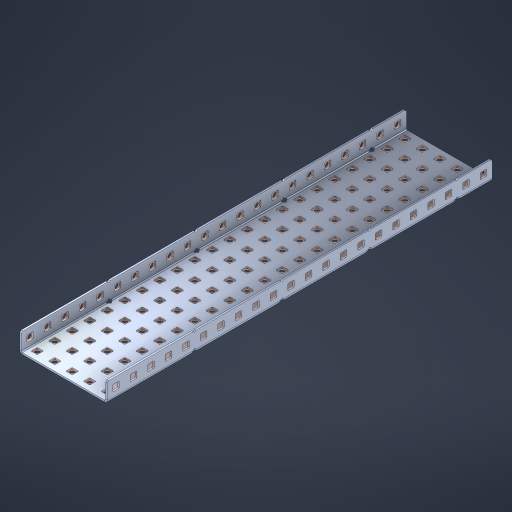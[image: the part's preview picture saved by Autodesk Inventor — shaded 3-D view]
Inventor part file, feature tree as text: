
AUTODESK INVENTOR PART (.ipt)
format: ipt  version: 2023 (Build 270158000, 158)  size: 1,778,176 bytes
history: native  units: in
note: dims shown in document units (in); Inventor stores cm internally (conversion verified against a paired STEP export)
features: other x159, extrude x153, sheet_metal_op x10, sketch x8, mirror x1, pattern_linear x1, chamfer x1
ambient origin geometry x8: Origin, YZ Plane, XZ Plane, XY Plane, X Axis, Y Axis, Z Axis, Center Point
bodies: Solid1 (feature_tree), Body (feature_tree)
feature tree (333):
  other  "Flange Pattern Plane"
  sheet_metal_op  "Flange Pattern"
  sheet_metal_op  "Body Pattern"
  other  "Arc Length"
  mirror  "Notch Mirror"
  pattern_linear  "Notch Pattern"  Spacing1=0.1875in  [1 undecoded]
  chamfer  "End Chamfer"
  extrude  "Half Cut"  Depth=0.0469in
  sketch  "Sketch1"  dims[d0=2.5in]
  other  "Plate1"
  sketch  "Sketch2"  dims[d1=11.0in]
  other  "Plate2"
  sheet_metal_op  "Bend1"
  sheet_metal_op  "Corner1"
  sketch  "Sketch3"  dims[d2=0.0469in]
  other  "Flange Pattern Sketch"
  sketch  "Sketch7"  dims[d3=0.0469in]
  other  "Srf1"
  other  "Srf2"
  sketch  "Sketch8"  dims[d4=0.0234in]
  sketch  "Sketch9"  dims[d5=0.0938in]
  other  "Srf91"
  sheet_metal_op  "Body Pattern Sketch"
  other  "Srf92"
  sketch  "Sketch13"  dims[d6=0.0469in]
  sketch  "Sketch14"  dims[d7=0.5in d8=90.0deg d9=0.0312in d10=0.1875in d11=0.0469in d12=0.0469in d16=0.182in d17=0.02in d18=0.0469in d19=0.0in d20=0.25in d21=0.25in d46=0.172in d47=1.0in d48=0.0in d49=0.182in d50=0.02in d51=0.25in d52=0.25in d53=0.0469in d54=0.0in d55=0.172in d56=1.0in d57=0.0in d60=8.6614in d62=0.5in d63=1.9685in d65=0.5in d85=0.1227in d86=0.1659in d88=0.04in d89=0.0469in d90=0.0in d91=0.04in d92=0.0491in d95=2.5in d96=0.04in d97=0.25in d98=45.0deg d101=0.0in d102=2.497in d131=2.5in d132=8.6614in d134=0.5in d139=0.5in]
  other  "Srf856"
  other  "Srf1310"
  other  "Srf1311"
  other  "Srf1312"
  other  "Srf1376"
  other  "Srf1377"
  other  "Srf1728"
  other  "Srf1755"
  other  "Srf1878"
  other  "Srf1879"
  other  "Srf1880"
  other  "Srf1881"
  other  "Srf1882"
  other  "Srf1883"
  other  "Srf1884"
  other  "Srf1885"
  other  "Srf1886"
  other  "Srf1887"
  other  "Srf1888"
  other  "Srf1889"
  other  "Srf1890"
  other  "Srf1891"
  other  "Srf1892"
  other  "Srf1893"
  other  "Srf1894"
  other  "Srf1895"
  other  "Srf1896"
  other  "Srf1897"
  other  "Srf1898"
  other  "Srf1899"
  other  "Srf1900"
  other  "Srf1901"
  other  "Srf1902"
  other  "Srf1903"
  other  "Srf1904"
  other  "Srf1905"
  other  "Srf1906"
  other  "Srf1942"
  other  "Srf1943"
  other  "Srf1944"
  other  "Srf1945"
  other  "Srf1946"
  other  "Srf1947"
  other  "Srf1948"
  other  "Srf1949"
  other  "Srf1950"
  other  "Srf1951"
  other  "Srf1952"
  other  "Srf1953"
  other  "Srf1954"
  other  "Srf1955"
  other  "Srf1956"
  other  "Srf1957"
  other  "Srf1958"
  other  "Srf1959"
  other  "Srf1960"
  other  "Srf1961"
  other  "Srf1962"
  other  "Srf1963"
  other  "Srf1964"
  other  "Srf1965"
  other  "Srf1966"
  other  "Srf1967"
  other  "Srf1968"
  other  "Srf1969"
  other  "Srf1970"
  other  "Srf2111"
  other  "Srf2112"
  other  "Srf2113"
  other  "Srf2114"
  other  "Srf2115"
  other  "Srf2116"
  other  "Srf2117"
  other  "Srf2118"
  other  "Srf2119"
  other  "Srf2146"
  other  "Srf2147"
  other  "Srf2148"
  other  "Srf2149"
  other  "Srf2150"
  other  "Srf2151"
  other  "Srf2152"
  other  "Srf2153"
  other  "Srf2154"
  other  "Srf2155"
  other  "Srf2156"
  other  "Srf2157"
  other  "Srf2158"
  other  "Srf2159"
  other  "Srf2160"
  other  "Srf2161"
  other  "Srf2162"
  other  "Srf2163"
  other  "Srf2164"
  other  "Srf2165"
  other  "Srf2166"
  other  "Srf2167"
  other  "Srf2168"
  other  "Srf2169"
  other  "Srf2170"
  other  "Srf2171"
  other  "Srf2172"
  other  "Srf2173"
  other  "Srf2174"
  other  "Srf2175"
  other  "Srf2176"
  other  "Srf2177"
  other  "Srf2178"
  other  "Srf2179"
  other  "Srf2180"
  other  "Srf2181"
  other  "Srf2182"
  other  "Srf2183"
  other  "Srf2184"
  other  "Srf2185"
  other  "Srf2186"
  other  "Srf2187"
  other  "Srf2188"
  other  "Srf2189"
  other  "Srf2190"
  other  "Srf2191"
  other  "Srf2192"
  other  "Srf2193"
  other  "Srf2194"
  other  "Srf2195"
  other  "Srf2196"
  other  "Srf2197"
  other  "Srf2198"
  other  "Srf2199"
  other  "Srf2200"
  other  "Srf2201"
  other  "Srf2202"
  other  "Srf2203"
  other  "Srf2204"
  other  "Srf2205"
  other  "Srf2206"
  other  "Srf2207"
  other  "Srf2208"
  other  "Srf2209"
  other  "Srf2210"
  other  "Srf2211"
  other  "Srf2212"
  other  "Srf2213"
  other  "Srf2214"
  other  "Srf2215"
  other  "Srf2216"
  other  "Srf2217"
  other  "Srf2218"
  other  "Srf2219"
  other  "Srf2220"
  sheet_metal_op  "Flange Stamp"
  sheet_metal_op  "Flange Circle"
  sheet_metal_op  "Body Stamp"
  sheet_metal_op  "Body Circle"
  sheet_metal_op  "Notch"
  extrude  "ExtrusionSrf2"  Depth=0.0469in
  extrude  "ExtrusionSrf92"  Depth=2.5in
  extrude  "ExtrusionSrf856"  Depth=0.02in
  extrude  "ExtrusionSrf1310"  Depth=0.0469in
  extrude  "ExtrusionSrf1311"  TaperAngle=0.0deg  [1 undecoded]
  extrude  "ExtrusionSrf1312"  Depth=0.25in
  extrude  "ExtrusionSrf1376"  Depth=0.25in
  extrude  "ExtrusionSrf1377"  Depth=2.5in
  extrude  "ExtrusionSrf1728"  Depth=2.5in TaperAngle=0.0deg
  extrude  "ExtrusionSrf1755"  Depth=2.5in
  extrude  "ExtrusionSrf1878"  Depth=0.02in
  extrude  "ExtrusionSrf1879"  Depth=0.25in
  extrude  "ExtrusionSrf1880"  Depth=0.25in
  extrude  "ExtrusionSrf1881"  Depth=0.0469in
  extrude  "ExtrusionSrf1882"  TaperAngle=0.0deg  [1 undecoded]
  extrude  "ExtrusionSrf1883"  Depth=2.5in
  extrude  "ExtrusionSrf1884"  Depth=2.5in TaperAngle=0.0deg
  extrude  "ExtrusionSrf1885"  Depth=2.5in
  extrude  "ExtrusionSrf1886"  Depth=2.5in
  extrude  "ExtrusionSrf1887"  Depth=2.5in
  extrude  "ExtrusionSrf1888"  Depth=2.5in
  extrude  "ExtrusionSrf1889"  Depth=2.5in
  extrude  "ExtrusionSrf1890"  Depth=0.0469in
  extrude  "ExtrusionSrf1891"  TaperAngle=0.0deg  [1 undecoded]
  extrude  "ExtrusionSrf1892"  Depth=2.5in
  extrude  "ExtrusionSrf1893"  Depth=2.5in
  extrude  "ExtrusionSrf1894"  Depth=2.5in
  extrude  "ExtrusionSrf1895"  Depth=0.25in TaperAngle=45.0deg
  extrude  "ExtrusionSrf1896"  TaperAngle=0.0deg  [1 undecoded]
  extrude  "ExtrusionSrf1897"  Depth=2.5in
  extrude  "ExtrusionSrf1898"  Depth=2.5in
  extrude  "ExtrusionSrf1899"  Depth=2.5in
  extrude  "ExtrusionSrf1900"  Depth=2.5in
  extrude  "ExtrusionSrf1901"  Depth=2.5in
  extrude  "ExtrusionSrf1902"  [1 undecoded]
  extrude  "ExtrusionSrf1903"  [1 undecoded]
  extrude  "ExtrusionSrf1904"  [1 undecoded]
  extrude  "ExtrusionSrf1905"  [1 undecoded]
  extrude  "ExtrusionSrf1906"  [1 undecoded]
  extrude  "ExtrusionSrf1942"  [1 undecoded]
  extrude  "ExtrusionSrf1943"  [1 undecoded]
  extrude  "ExtrusionSrf1944"  [1 undecoded]
  extrude  "ExtrusionSrf1945"  [1 undecoded]
  extrude  "ExtrusionSrf1946"  [1 undecoded]
  extrude  "ExtrusionSrf1947"  [1 undecoded]
  extrude  "ExtrusionSrf1948"  [1 undecoded]
  extrude  "ExtrusionSrf1949"  [1 undecoded]
  extrude  "ExtrusionSrf1950"  [1 undecoded]
  extrude  "ExtrusionSrf1951"  [1 undecoded]
  extrude  "ExtrusionSrf1952"  [1 undecoded]
  extrude  "ExtrusionSrf1953"  [1 undecoded]
  extrude  "ExtrusionSrf1954"  [1 undecoded]
  extrude  "ExtrusionSrf1955"  [1 undecoded]
  extrude  "ExtrusionSrf1956"  [1 undecoded]
  extrude  "ExtrusionSrf1957"  [1 undecoded]
  extrude  "ExtrusionSrf1958"  [1 undecoded]
  extrude  "ExtrusionSrf1959"  [1 undecoded]
  extrude  "ExtrusionSrf1960"  [1 undecoded]
  extrude  "ExtrusionSrf1961"  [1 undecoded]
  extrude  "ExtrusionSrf1962"  [1 undecoded]
  extrude  "ExtrusionSrf1963"  [1 undecoded]
  extrude  "ExtrusionSrf1964"  [1 undecoded]
  extrude  "ExtrusionSrf1965"  [1 undecoded]
  extrude  "ExtrusionSrf1966"  [1 undecoded]
  extrude  "ExtrusionSrf1967"  [1 undecoded]
  extrude  "ExtrusionSrf1968"  [1 undecoded]
  extrude  "ExtrusionSrf1969"  [1 undecoded]
  extrude  "ExtrusionSrf1970"  [1 undecoded]
  extrude  "ExtrusionSrf2111"  [1 undecoded]
  extrude  "ExtrusionSrf2112"  [1 undecoded]
  extrude  "ExtrusionSrf2113"  [1 undecoded]
  extrude  "ExtrusionSrf2114"  [1 undecoded]
  extrude  "ExtrusionSrf2115"  [1 undecoded]
  extrude  "ExtrusionSrf2116"  [1 undecoded]
  extrude  "ExtrusionSrf2117"  [1 undecoded]
  extrude  "ExtrusionSrf2118"  [1 undecoded]
  extrude  "ExtrusionSrf2119"  [1 undecoded]
  extrude  "ExtrusionSrf2146"  [1 undecoded]
  extrude  "ExtrusionSrf2147"  [1 undecoded]
  extrude  "ExtrusionSrf2148"  [1 undecoded]
  extrude  "ExtrusionSrf2149"  [1 undecoded]
  extrude  "ExtrusionSrf2150"  [1 undecoded]
  extrude  "ExtrusionSrf2151"  [1 undecoded]
  extrude  "ExtrusionSrf2152"  [1 undecoded]
  extrude  "ExtrusionSrf2153"  [1 undecoded]
  extrude  "ExtrusionSrf2154"  [1 undecoded]
  extrude  "ExtrusionSrf2155"  [1 undecoded]
  extrude  "ExtrusionSrf2156"  [1 undecoded]
  extrude  "ExtrusionSrf2157"  [1 undecoded]
  extrude  "ExtrusionSrf2158"  [1 undecoded]
  extrude  "ExtrusionSrf2159"  [1 undecoded]
  extrude  "ExtrusionSrf2160"  [1 undecoded]
  extrude  "ExtrusionSrf2161"  [1 undecoded]
  extrude  "ExtrusionSrf2162"  [1 undecoded]
  extrude  "ExtrusionSrf2163"  [1 undecoded]
  extrude  "ExtrusionSrf2164"  [1 undecoded]
  extrude  "ExtrusionSrf2165"  [1 undecoded]
  extrude  "ExtrusionSrf2166"  [1 undecoded]
  extrude  "ExtrusionSrf2167"  [1 undecoded]
  extrude  "ExtrusionSrf2168"  [1 undecoded]
  extrude  "ExtrusionSrf2169"  [1 undecoded]
  extrude  "ExtrusionSrf2170"  [1 undecoded]
  extrude  "ExtrusionSrf2171"  [1 undecoded]
  extrude  "ExtrusionSrf2172"  [1 undecoded]
  extrude  "ExtrusionSrf2173"  [1 undecoded]
  extrude  "ExtrusionSrf2174"  [1 undecoded]
  extrude  "ExtrusionSrf2175"  [1 undecoded]
  extrude  "ExtrusionSrf2176"  [1 undecoded]
  extrude  "ExtrusionSrf2177"  [1 undecoded]
  extrude  "ExtrusionSrf2178"  [1 undecoded]
  extrude  "ExtrusionSrf2179"  [1 undecoded]
  extrude  "ExtrusionSrf2180"  [1 undecoded]
  extrude  "ExtrusionSrf2181"  [1 undecoded]
  extrude  "ExtrusionSrf2182"  [1 undecoded]
  extrude  "ExtrusionSrf2183"  [1 undecoded]
  extrude  "ExtrusionSrf2184"  [1 undecoded]
  extrude  "ExtrusionSrf2185"  [1 undecoded]
  extrude  "ExtrusionSrf2186"  [1 undecoded]
  extrude  "ExtrusionSrf2187"  [1 undecoded]
  extrude  "ExtrusionSrf2188"  [1 undecoded]
  extrude  "ExtrusionSrf2189"  [1 undecoded]
  extrude  "ExtrusionSrf2190"  [1 undecoded]
  extrude  "ExtrusionSrf2191"  [1 undecoded]
  extrude  "ExtrusionSrf2192"  [1 undecoded]
  extrude  "ExtrusionSrf2193"  [1 undecoded]
  extrude  "ExtrusionSrf2194"  [1 undecoded]
  extrude  "ExtrusionSrf2195"  [1 undecoded]
  extrude  "ExtrusionSrf2196"  [1 undecoded]
  extrude  "ExtrusionSrf2197"  [1 undecoded]
  extrude  "ExtrusionSrf2198"  [1 undecoded]
  extrude  "ExtrusionSrf2199"  [1 undecoded]
  extrude  "ExtrusionSrf2200"  [1 undecoded]
  extrude  "ExtrusionSrf2201"  [1 undecoded]
  extrude  "ExtrusionSrf2202"  [1 undecoded]
  extrude  "ExtrusionSrf2203"  [1 undecoded]
  extrude  "ExtrusionSrf2204"  [1 undecoded]
  extrude  "ExtrusionSrf2205"  [1 undecoded]
  extrude  "ExtrusionSrf2206"  [1 undecoded]
  extrude  "ExtrusionSrf2207"  [1 undecoded]
  extrude  "ExtrusionSrf2208"  [1 undecoded]
  extrude  "ExtrusionSrf2209"  [1 undecoded]
  extrude  "ExtrusionSrf2210"  [1 undecoded]
  extrude  "ExtrusionSrf2211"  [1 undecoded]
  extrude  "ExtrusionSrf2212"  [1 undecoded]
  extrude  "ExtrusionSrf2213"  [1 undecoded]
  extrude  "ExtrusionSrf2214"  [1 undecoded]
  extrude  "ExtrusionSrf2215"  [1 undecoded]
  extrude  "ExtrusionSrf2216"  [1 undecoded]
  extrude  "ExtrusionSrf2217"  [1 undecoded]
  extrude  "ExtrusionSrf2218"  [1 undecoded]
  extrude  "ExtrusionSrf2219"  [1 undecoded]
  extrude  "ExtrusionSrf2220"  [1 undecoded]
note: 123 required parameter values undecoded (feature->parameter linkage not recoverable at this tier; creation-order binding heuristic only, values carry confidence <= 0.55)
